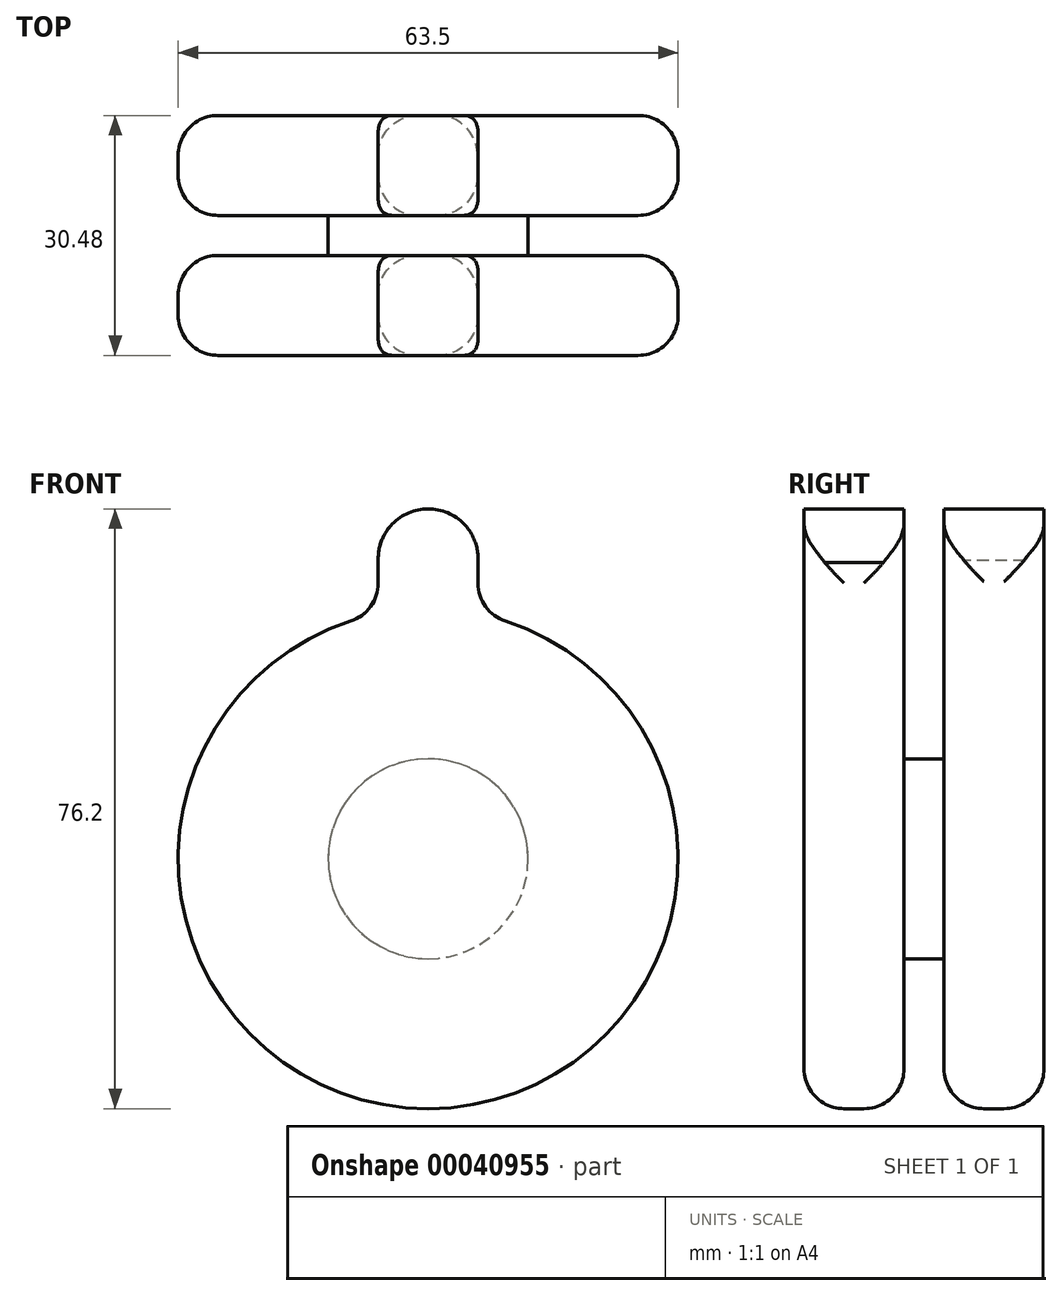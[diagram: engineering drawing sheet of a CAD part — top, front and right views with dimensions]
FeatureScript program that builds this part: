
annotation { "Feature Type Name" : "Feature", "Feature Type Description" : "" }
export const myFeature = defineFeature(function(context is Context, id is Id, definition is map)
    precondition{}
    {
        {
            var Q0;
            Q0=qCreatedBy(makeId("Front.planeOp"),FACE);
            var sketch = newSketch(context, id + "F0", { "sketchPlane" : qUnion([Q0])});
            skCircle(sketch, "E0", {"center": v(0, 0) * mm, "radius": 31.75 * mm});
            skCircle(sketch, "E1", {"center": v(0, 38.1) * mm, "radius": 6.35 * mm});
            skLineSegment(sketch, "E2", {"start": v(-6.34, 37.72) * mm, "end": v(-6.34, 31.11) * mm});
            skLineSegment(sketch, "E3", {"start": v(6.33, 31.11) * mm, "end": v(6.33, 37.64) * mm});
            skSolve(sketch);
        }
        {
            var Q0;
            Q0 = qSketchRegion(id + "F0", true);
            extrude(context, id + "F1", {"entities" : qUnion([Q0]), "depth" : 12.7 * mm});
        }
        {
            var Q0;
            Q0=makeQuery(id+"F1.opExtrude","SWEPT_FACE",FACE,{"disambiguationData":[OSD([sQuery(id+"F0.wireOp",EDGE,"E0")])]});
            fillet(context, id + "F2", {"entities" : qUnion([Q0]), "radius" : 5.08 * mm, "tangentPropagation" : true, "allowEdgeOverflow" : false});
        }
        {
            var Q0;
            Q0=makeQuery(id+"F1.opExtrude","CAP_FACE",FACE,{"disambiguationData":[OSD([sQuery(id+"F0.wireOp",EDGE,"E0")])],"isStart":true});
            var sketch = newSketch(context, id + "F3", { "sketchPlane" : qUnion([Q0])});
            skCircle(sketch, "E4", {"center": v(0, 0) * mm, "radius": 12.7 * mm});
            skSolve(sketch);
        }
        {
            var Q0;
            Q0 = qSketchRegion(id + "F3", true);
            extrude(context, id + "F4", {"entities" : qUnion([Q0]), "operationType" : NewBodyOperationType.ADD, "depth" : 5.08 * mm});
        }
        {
            var Q0;
            Q0=makeQuery(id+"F4.opExtrude","CAP_FACE",FACE,{"disambiguationData":[OSD([sQuery(id+"F3.wireOp",EDGE,"E4")])],"isStart":false});
            var sketch = newSketch(context, id + "F5", { "sketchPlane" : qUnion([Q0])});
            skCircle(sketch, "E5", {"center": v(0, 0) * mm, "radius": 31.75 * mm});
            skCircle(sketch, "E6", {"center": v(0, 38.1) * mm, "radius": 6.35 * mm});
            skLineSegment(sketch, "E7", {"start": v(-6.15, 31.15) * mm, "end": v(-6.35, 37.91) * mm});
            skLineSegment(sketch, "E8", {"start": v(6.35, 37.91) * mm, "end": v(6.35, 31.1) * mm});
            skSolve(sketch);
        }
        {
            var Q0;
            Q0 = qSketchRegion(id + "F5", true);
            extrude(context, id + "F6", {"entities" : qUnion([Q0]), "operationType" : NewBodyOperationType.ADD, "depth" : 12.7 * mm});
        }
        {
            var Q0;
            Q0=makeQuery(id+"F6.opExtrude","SWEPT_FACE",FACE,{"disambiguationData":[OSD([sQuery(id+"F5.wireOp",EDGE,"E5")])]});
            fillet(context, id + "F7", {"entities" : qUnion([Q0]), "radius" : 5.08 * mm, "tangentPropagation" : true, "allowEdgeOverflow" : false});
        }
    });
